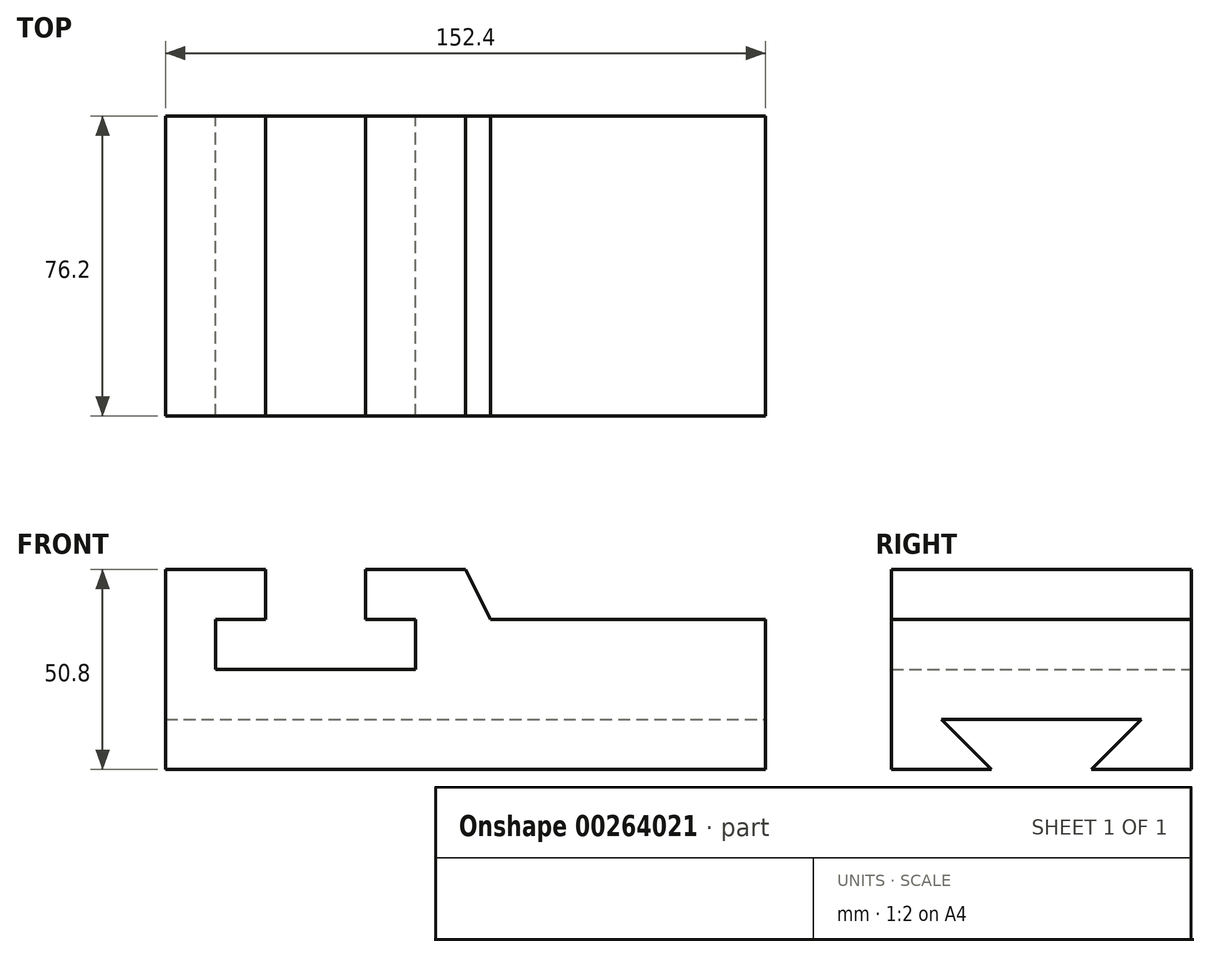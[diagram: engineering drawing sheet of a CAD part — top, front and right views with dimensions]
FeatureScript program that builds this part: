
annotation { "Feature Type Name" : "Feature", "Feature Type Description" : "" }
export const myFeature = defineFeature(function(context is Context, id is Id, definition is map)
    precondition{}
    {
        {
            var Q0;
            Q0=qCreatedBy(makeId("Front.planeOp"),FACE);
            var sketch = newSketch(context, id + "F0", { "sketchPlane" : qUnion([Q0])});
            skLineSegment(sketch, "E0", {"start": v(-76.2, 0) * mm, "end": v(76.2, 0) * mm});
            skLineSegment(sketch, "E1", {"start": v(76.2, 0) * mm, "end": v(76.2, 38.1) * mm});
            skLineSegment(sketch, "E2", {"start": v(76.2, 38.1) * mm, "end": v(6.35, 38.1) * mm});
            skLineSegment(sketch, "E3", {"start": v(0, 50.8) * mm, "end": v(6.35, 38.1) * mm});
            skLineSegment(sketch, "E4", {"start": v(0, 50.8) * mm, "end": v(-25.4, 50.8) * mm});
            skLineSegment(sketch, "E5", {"start": v(-25.4, 50.8) * mm, "end": v(-25.4, 38.1) * mm});
            skLineSegment(sketch, "E6", {"start": v(-25.4, 38.1) * mm, "end": v(-12.7, 38.1) * mm});
            skLineSegment(sketch, "E7", {"start": v(-12.7, 38.1) * mm, "end": v(-12.7, 25.4) * mm});
            skLineSegment(sketch, "E8", {"start": v(-12.7, 25.4) * mm, "end": v(-63.5, 25.4) * mm});
            skLineSegment(sketch, "E9", {"start": v(-63.5, 25.4) * mm, "end": v(-63.5, 38.1) * mm});
            skLineSegment(sketch, "E10", {"start": v(-63.5, 38.1) * mm, "end": v(-50.8, 38.1) * mm});
            skLineSegment(sketch, "E11", {"start": v(-50.8, 38.1) * mm, "end": v(-50.8, 50.8) * mm});
            skLineSegment(sketch, "E12", {"start": v(-50.8, 50.8) * mm, "end": v(-76.2, 50.8) * mm});
            skLineSegment(sketch, "E13", {"start": v(-76.2, 50.8) * mm, "end": v(-76.2, 0) * mm});
            skSolve(sketch);
        }
        {
            var Q0;
            Q0=makeQuery(id+"F0.imprint","IMPRINT",FACE,{"disambiguationData":[TD([[makeQuery(id+"F0.imprint","IMPRINT",EDGE,{"derivedFrom":sQuery(id+"F0.wireOp",EDGE,"E0")}),1.0]])]});
            extrude(context, id + "F1", {"entities" : qUnion([Q0]), "depth" : 38.1 * mm});
        }
        {
            var Q0;
            Q0=makeQuery(id+"F1.opExtrude","CAP_FACE",FACE,{"disambiguationData":[OSD([sQuery(id+"F0.wireOp",EDGE,"E0"),sQuery(id+"F0.wireOp",EDGE,"E1"),sQuery(id+"F0.wireOp",EDGE,"E2"),sQuery(id+"F0.wireOp",EDGE,"E3"),sQuery(id+"F0.wireOp",EDGE,"E4"),sQuery(id+"F0.wireOp",EDGE,"E5"),sQuery(id+"F0.wireOp",EDGE,"E6"),sQuery(id+"F0.wireOp",EDGE,"E7"),sQuery(id+"F0.wireOp",EDGE,"E8"),sQuery(id+"F0.wireOp",EDGE,"E9"),sQuery(id+"F0.wireOp",EDGE,"E10"),sQuery(id+"F0.wireOp",EDGE,"E11"),sQuery(id+"F0.wireOp",EDGE,"E12"),sQuery(id+"F0.wireOp",EDGE,"E13")])],"isStart":true});
            extrude(context, id + "F2", {"entities" : qUnion([Q0]), "operationType" : NewBodyOperationType.ADD, "depth" : 38.1 * mm});
        }
        {
            var Q0;
            {var subQ0=sQuery(id+"F0.wireOp",EDGE,"E1");Q0=makeQuery(id+"F2.boolean.opBoolean","MERGE",FACE,{"derivedFrom":[makeQuery(id+"F1.opExtrude","SWEPT_FACE",FACE,{"disambiguationData":[OSD([subQ0])]}),makeQuery(id+"F2.opExtrude","SWEPT_FACE",FACE,{"disambiguationData":[OSD([subQ0])]})]});}
            var sketch = newSketch(context, id + "F3", { "sketchPlane" : qUnion([Q0])});
            skLineSegment(sketch, "E14", {"start": v(-25.4, 12.7) * mm, "end": v(-12.7, 0) * mm});
            skLineSegment(sketch, "E15", {"start": v(25.4, 12.7) * mm, "end": v(12.7, 0) * mm});
            skLineSegment(sketch, "E16", {"start": v(-25.4, 12.7) * mm, "end": v(25.4, 12.7) * mm});
            skLineSegment(sketch, "E17", {"start": v(-12.7, 0) * mm, "end": v(12.7, 0) * mm});
            skSolve(sketch);
        }
        {
            var Q0;
            Q0=makeQuery(id+"F3.imprint","IMPRINT",FACE,{"disambiguationData":[TD([[makeQuery(id+"F3.imprint","IMPRINT",EDGE,{"derivedFrom":sQuery(id+"F3.wireOp",EDGE,"E14")}),1.0]])]});
            extrude(context, id + "F4", {"entities" : qUnion([Q0]), "operationType" : NewBodyOperationType.REMOVE, "oppositeDirection" : true, "depth" : 152.4 * mm});
        }
    });
